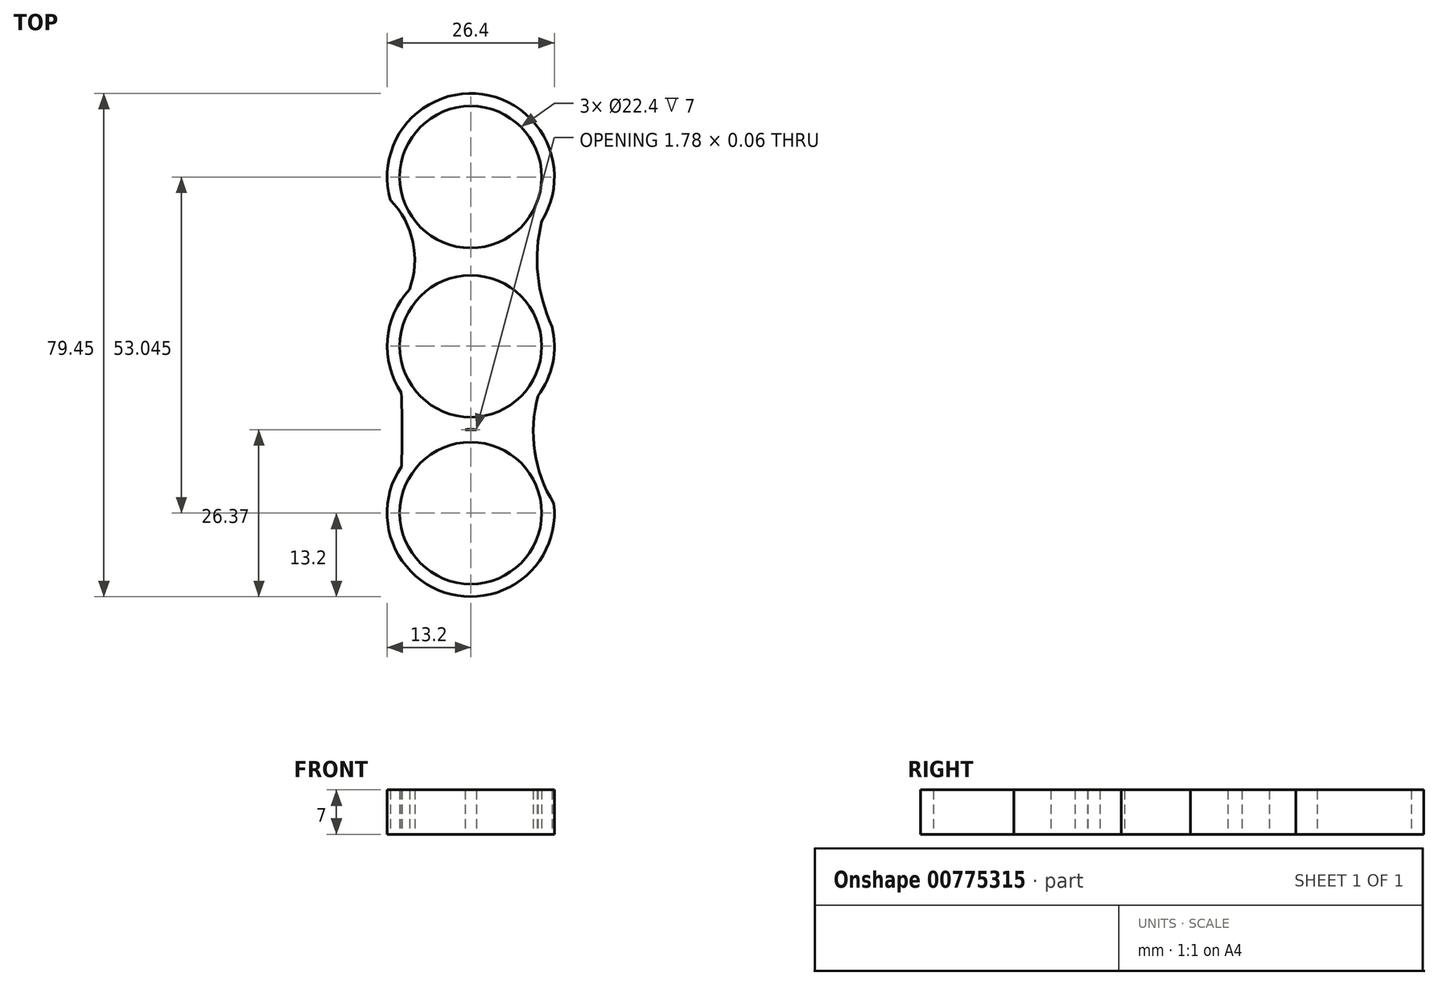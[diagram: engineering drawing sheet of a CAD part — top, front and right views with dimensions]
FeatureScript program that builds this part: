
annotation { "Feature Type Name" : "Feature", "Feature Type Description" : "" }
export const myFeature = defineFeature(function(context is Context, id is Id, definition is map)
    precondition{}
    {
        {
            var Q0;
            Q0=qCreatedBy(makeId("Top.planeOp"),FACE);
            var sketch = newSketch(context, id + "F0", { "sketchPlane" : qUnion([Q0])});
            skCircle(sketch, "E0", {"center": v(0, 0) * mm, "radius": 11.2 * mm});
            skCircle(sketch, "E1", {"center": v(0, 0) * mm, "radius": 13.2 * mm});
            skCircle(sketch, "E2", {"center": v(0, 26.7) * mm, "radius": 11.2 * mm});
            skCircle(sketch, "E3", {"center": v(0, 26.7) * mm, "radius": 13.2 * mm});
            skCircle(sketch, "E4", {"center": v(0, -26.34) * mm, "radius": 11.2 * mm});
            skCircle(sketch, "E5", {"center": v(0, -26.34) * mm, "radius": 13.2 * mm});
            skArc(sketch, "E6", {"start": v(11.2, 19.74) * mm, "mid": v(10.6, 11.28) * mm, "end": v(12.83, 3.1) * mm});
            skArc(sketch, "E7", {"start": v(10.6, -7.86) * mm, "mid": v(10.1, -16.6) * mm, "end": v(13.11, -24.83) * mm});
            skArc(sketch, "E8", {"start": v(-9.67, 8.98) * mm, "mid": v(-9.15, 16.47) * mm, "end": v(-12.7, 23.09) * mm});
            skArc(sketch, "E9", {"start": v(-10.95, -18.96) * mm, "mid": v(-10.83, -13.16) * mm, "end": v(-10.96, -7.35) * mm});
            skSolve(sketch);
        }
        {
            var Q0;
            Q0=makeQuery(id+"F0.imprint","IMPRINT",FACE,{"disambiguationData":[TD([[makeQuery(id+"F0.imprint","IMPRINT",EDGE,{"derivedFrom":sQuery(id+"F0.wireOp",EDGE,"E2")}),-1.0]])]});
            var Q1;
            Q1=makeQuery(id+"F0.imprint","IMPRINT",FACE,{"disambiguationData":[TD([[makeQuery(id+"F0.imprint","IMPRINT",EDGE,{"derivedFrom":sQuery(id+"F0.wireOp",EDGE,"E4")}),-1.0]])]});
            var Q2;
            {var subQ0=sQuery(id+"F0.wireOp",EDGE,"E8");var subQ1=sQuery(id+"F0.wireOp",EDGE,"E1");var subQ2=makeQuery(id+"F0.imprint","INTERSECT",VERTEX,{"derivedFrom":[subQ1,subQ0]});Q2=makeQuery(id+"F0.imprint","IMPRINT",FACE,{"disambiguationData":[TD([[makeQuery(id+"F0.imprint","IMPRINT",EDGE,{"disambiguationData":[TD([[subQ2,1.0]])],"derivedFrom":subQ1}),-1.0]])]});}
            var Q3;
            {var subQ0=sQuery(id+"F0.wireOp",EDGE,"E7");var subQ1=sQuery(id+"F0.wireOp",EDGE,"E1");var subQ2=makeQuery(id+"F0.imprint","INTERSECT",VERTEX,{"derivedFrom":[subQ1,subQ0]});Q3=makeQuery(id+"F0.imprint","IMPRINT",FACE,{"disambiguationData":[TD([[makeQuery(id+"F0.imprint","IMPRINT",EDGE,{"disambiguationData":[TD([[subQ2,1.0]])],"derivedFrom":subQ1}),-1.0]])]});}
            var Q4;
            {var subQ0=sQuery(id+"F0.wireOp",EDGE,"E9");Q4=makeQuery(id+"F0.imprint","IMPRINT",FACE,{"disambiguationData":[TD([[makeQuery(id+"F0.imprint","IMPRINT",EDGE,{"derivedFrom":subQ0}),-1.0]])]});}
            var Q5;
            Q5=makeQuery(id+"F0.imprint","IMPRINT",FACE,{"disambiguationData":[TD([[makeQuery(id+"F0.imprint","IMPRINT",EDGE,{"derivedFrom":sQuery(id+"F0.wireOp",EDGE,"E0")}),-1.0]])]});
            extrude(context, id + "F1", {"entities" : qUnion([Q0, Q1, Q2, Q3, Q4, Q5]), "depth" : 7 * mm, "offsetDistance" : 25 * mm});
        }
    });
